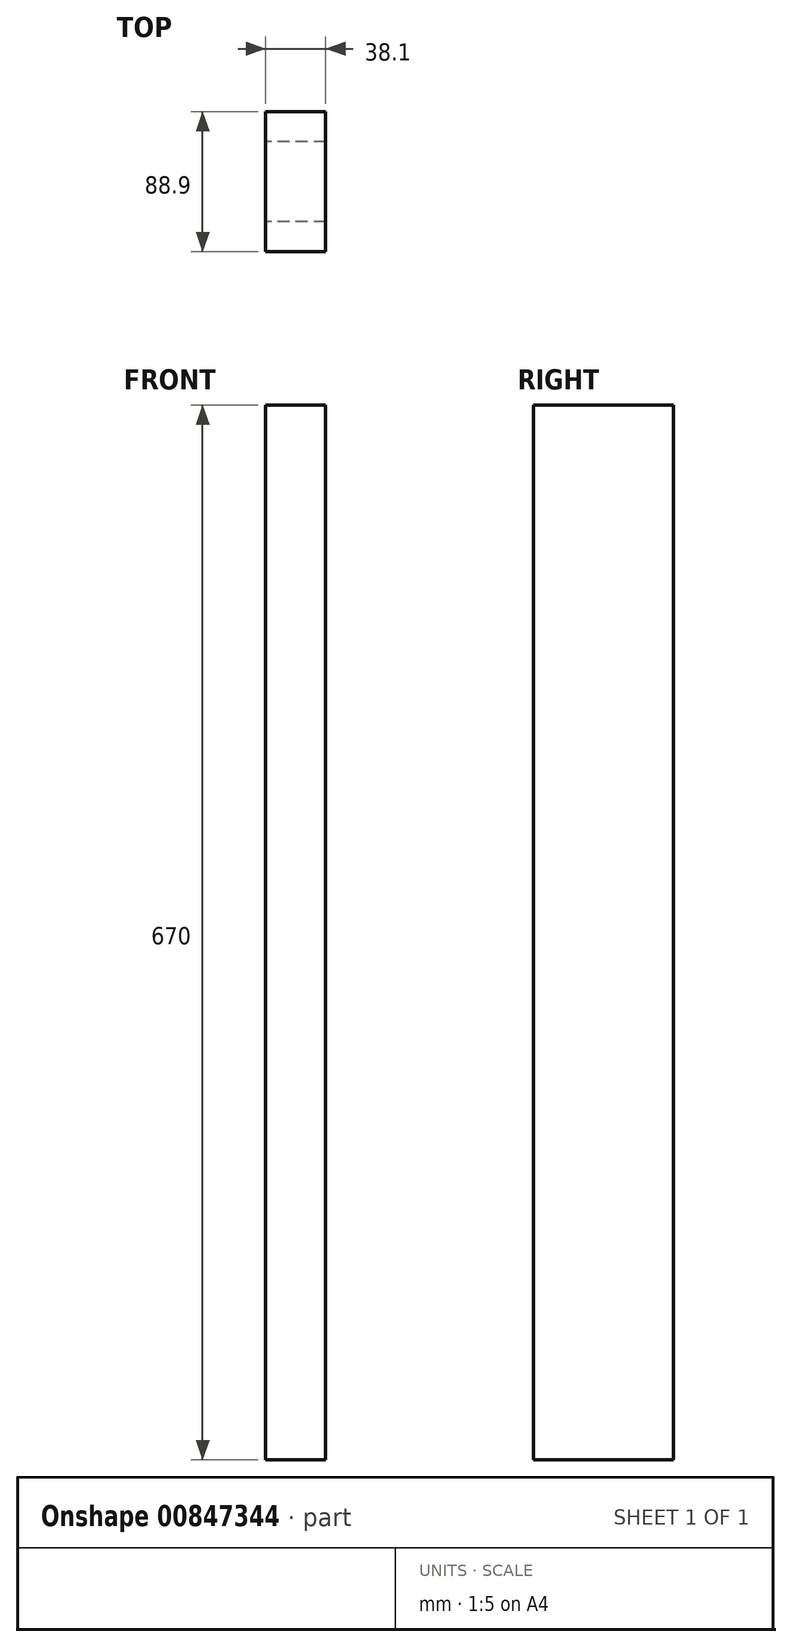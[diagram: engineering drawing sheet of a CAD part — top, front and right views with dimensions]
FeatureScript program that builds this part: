
annotation { "Feature Type Name" : "Feature", "Feature Type Description" : "" }
export const myFeature = defineFeature(function(context is Context, id is Id, definition is map)
    precondition{}
    {
        {
            var Q0;
            Q0=qCreatedBy(makeId("Top.planeOp"),FACE);
            var sketch = newSketch(context, id + "F0", { "sketchPlane" : qUnion([Q0])});
            skLineSegment(sketch, "E0.bottom", {"start": v(0, 0) * mm, "end": v(38.1, 0) * mm});
            skLineSegment(sketch, "E0.top", {"start": v(0, 88.9) * mm, "end": v(38.1, 88.9) * mm});
            skLineSegment(sketch, "E0.left", {"start": v(0, 0) * mm, "end": v(0, 88.9) * mm});
            skLineSegment(sketch, "E0.right", {"start": v(38.1, 0) * mm, "end": v(38.1, 88.9) * mm});
            skSolve(sketch);
        }
        {
            var Q0;
            Q0=makeQuery(id+"F0.imprint","IMPRINT",FACE,{"disambiguationData":[TD([[makeQuery(id+"F0.imprint","IMPRINT",EDGE,{"derivedFrom":sQuery(id+"F0.wireOp",EDGE,"E0.bottom")}),1.0]])]});
            extrude(context, id + "F1", {"entities" : qUnion([Q0]), "depth" : 670 * mm - 3 / 101.6 * mm, "offsetDistance" : 25 * mm});
        }
        {
            var Q0;
            Q0=makeQuery(id+"F1.opExtrude","CAP_FACE",FACE,{"disambiguationData":[OSD([sQuery(id+"F0.wireOp",EDGE,"E0.bottom"),sQuery(id+"F0.wireOp",EDGE,"E0.top"),sQuery(id+"F0.wireOp",EDGE,"E0.left"),sQuery(id+"F0.wireOp",EDGE,"E0.right")])],"isStart":true});
            var sketch = newSketch(context, id + "F2", { "sketchPlane" : qUnion([Q0])});
            skLineSegment(sketch, "E1.bottom", {"start": v(38.1, -19.05) * mm, "end": v(0, -19.05) * mm});
            skLineSegment(sketch, "E1.top", {"start": v(38.1, -69.85) * mm, "end": v(0, -69.85) * mm});
            skLineSegment(sketch, "E1.left", {"start": v(38.1, -19.05) * mm, "end": v(38.1, -69.85) * mm});
            skLineSegment(sketch, "E1.right", {"start": v(0, -19.05) * mm, "end": v(0, -69.85) * mm});
            skSolve(sketch);
        }
        {
            var Q0;
            Q0=makeQuery(id+"F2.imprint","IMPRINT",FACE,{"disambiguationData":[TD([[makeQuery(id+"F2.imprint","IMPRINT",EDGE,{"derivedFrom":sQuery(id+"F2.wireOp",EDGE,"E1.bottom")}),1.0]])]});
            extrude(context, id + "F3", {"entities" : qUnion([Q0]), "operationType" : NewBodyOperationType.ADD, "depth" : 3 / 101.6 * mm, "offsetDistance" : 25 * mm});
        }
    });
